# Revit family: Bicycle-Rack_Dero_Arc
name_source: partatom
category: Generic Models
units: mm (PartAtom-declared; Revit-internal decimal feet)

## family parameters
Can host rebar = No
Classification Number = 23.40.10.11.11
Cut with Voids When Loaded = No
Host = Face
Maintain Annotation Orientation = No
Part Type = Normal
Room Calculation Point = No
Round Connector Dimension = Use Diameter
Shared = No

## types (2) — shared parameters
Assembly Code = E1090900
Available Options = Galvanized / Powder Coat / Stainless / Thermoplastic
CAD Details = https://www.arcat.com
Capacity = 2 Bikes
Default Elevation = 0' - 0"
Keynote = 12 93 13
Manufacturer = Dero Bike Rack Co.
Product Page URL = https://www.arcat.com
Specification = https://www.arcat.com
URL = http://www.dero.com
Unit Depth = 0' - 2"
Unit Width = 3' - 6"
radius = 1' - 9"
zero-valued in all types: Cost

## per-type parameters (varying)
| type | Description | InGround | Model | Unit Height |
| InGround Mount | Dero InGround Bike Rack - Arc as Specified | Yes | Arc InGround | 3' - 0 7/8" |
| Surface Mount | Dero Surface Mounted Bike Rack - Arc as Specified | No | Arc Surface | 3' - 1 1/4" |

type visibility flags (boolean, named after types; folded from table):
- InGround Mount: Yes: (none)
- Surface Mount: Yes: Surface Mount

## geometry (parser evidence)
native form markers: Sweep x2
no freeform markers — native parametric forms only
